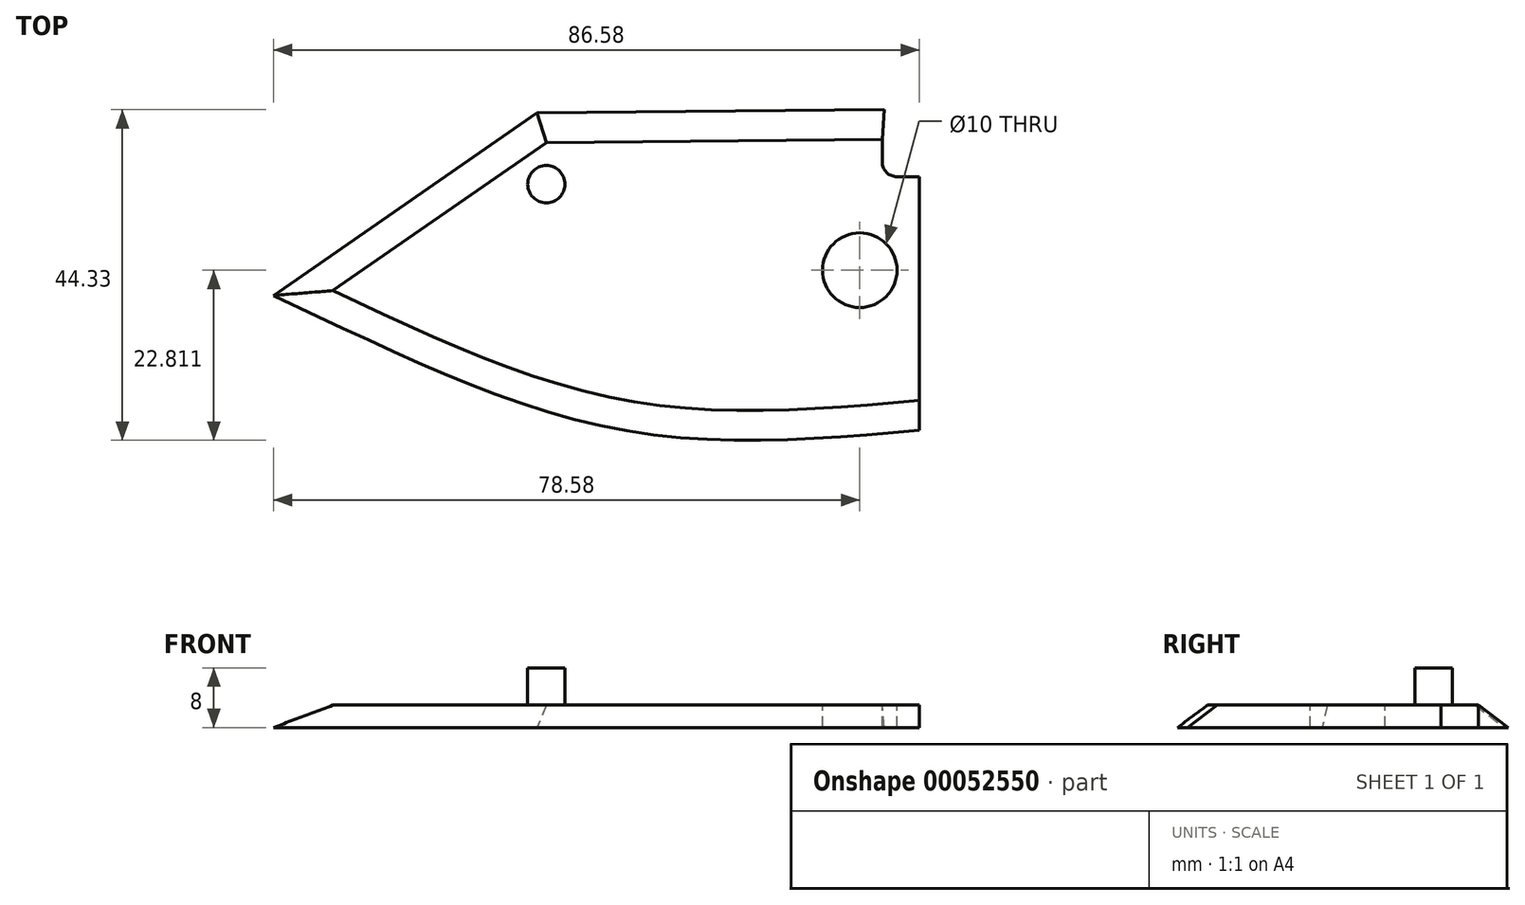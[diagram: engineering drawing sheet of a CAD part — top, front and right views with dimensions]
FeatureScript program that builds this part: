
annotation { "Feature Type Name" : "Feature", "Feature Type Description" : "" }
export const myFeature = defineFeature(function(context is Context, id is Id, definition is map)
    precondition{}
    {
        {
            var Q0;
            Q0=qCreatedBy(makeId("Top.planeOp"),FACE);
            var sketch = newSketch(context, id + "F0", { "sketchPlane" : qUnion([Q0])});
            skLineSegment(sketch, "E0", {"start": v(-5, 35) * mm, "end": v(-50, 34.58) * mm});
            skLineSegment(sketch, "E1", {"start": v(-50, 34.58) * mm, "end": v(-78.63, 14.74) * mm});
            skFitSpline(sketch, "E2", {"points": [v(-78.63, 14.74) * mm, v(-39.25, 0) * mm, v(0, 0) * mm], "startDerivative": vector(77.58, -36.48) * mm, "endDerivative": vector(80.57, 7.12) * mm});
            skLineSegment(sketch, "E3", {"start": v(0, 0) * mm, "end": v(0, 30) * mm});
            skLineSegment(sketch, "E4", {"start": v(0, 30) * mm, "end": v(-3, 30) * mm});
            skLineSegment(sketch, "E5", {"start": v(-5, 32) * mm, "end": v(-5, 35) * mm});
            skPoint(sketch, "E6.visualSharp", {"position": v(-5, 30) * mm});
            skArc(sketch, "E6.filletArc", {"start": v(-5, 32) * mm, "mid": v(-4.41, 30.59) * mm, "end": v(-3, 30) * mm});
            skSolve(sketch);
        }
        {
            var Q0;
            Q0=qCreatedBy(makeId("Right.planeOp"),FACE);
            var sketch = newSketch(context, id + "F1", { "sketchPlane" : qUnion([Q0])});
            skLineSegment(sketch, "E7", {"start": v(0, 0) * mm, "end": v(-4, 0) * mm});
            skLineSegment(sketch, "E8", {"start": v(-4, 0) * mm, "end": v(0, 3) * mm});
            skLineSegment(sketch, "E9", {"start": v(0, 0) * mm, "end": v(0, 3) * mm});
            skSolve(sketch);
        }
        {
            var Q0;
            Q0=makeQuery(id+"F1.imprint","IMPRINT",FACE,{"disambiguationData":[TD([[makeQuery(id+"F1.imprint","IMPRINT",EDGE,{"derivedFrom":sQuery(id+"F1.wireOp",EDGE,"E7")}),-1.0]])]});
            var Q1;
            Q1=sQuery(id+"F0.wireOp",EDGE,"E2");
            var Q2;
            Q2=sQuery(id+"F0.wireOp",EDGE,"E1");
            var Q3;
            Q3=sQuery(id+"F0.wireOp",EDGE,"E0");
            sweep(context, id + "F2", {"profiles" : qUnion([Q0]), "path" : qUnion([Q1, Q2, Q3])});
        }
        {
            var Q0;
            Q0 = qSketchRegion(id + "F0", true);
            extrude(context, id + "F3", {"entities" : qUnion([Q0]), "operationType" : NewBodyOperationType.ADD, "depth" : 3 * mm});
        }
        {
            var Q0;
            Q0=makeQuery(id+"F3.opExtrude","CAP_FACE",FACE,{"disambiguationData":[OSD([sQuery(id+"F0.wireOp",EDGE,"ca5b04ca-4ff3-4a42-8b16-5efeb9b8746d"),sQuery(id+"F0.wireOp",EDGE,"E0"),sQuery(id+"F0.wireOp",EDGE,"E1"),sQuery(id+"F0.wireOp",EDGE,"E2")])],"isStart":false});
            var sketch = newSketch(context, id + "F4", { "sketchPlane" : qUnion([Q0])});
            skCircle(sketch, "E10", {"center": v(-8, 17.47) * mm, "radius": 5 * mm});
            skSolve(sketch);
        }
        {
            var Q0;
            Q0=makeQuery(id+"F4.imprint","IMPRINT",FACE,{"disambiguationData":[TD([[makeQuery(id+"F4.imprint","IMPRINT",EDGE,{"derivedFrom":sQuery(id+"F4.wireOp",EDGE,"E10")}),1.0]])]});
            extrude(context, id + "F5", {"entities" : qUnion([Q0]), "operationType" : NewBodyOperationType.REMOVE, "oppositeDirection" : true, "depth" : 25 * mm});
        }
        {
            var Q0;
            Q0=makeQuery(id+"F3.opExtrude","CAP_FACE",FACE,{"disambiguationData":[OSD([sQuery(id+"F0.wireOp",EDGE,"ca5b04ca-4ff3-4a42-8b16-5efeb9b8746d"),sQuery(id+"F0.wireOp",EDGE,"E0"),sQuery(id+"F0.wireOp",EDGE,"E1"),sQuery(id+"F0.wireOp",EDGE,"E2")])],"isStart":false});
            var sketch = newSketch(context, id + "F6", { "sketchPlane" : qUnion([Q0])});
            skCircle(sketch, "E11", {"center": v(-50, 29) * mm, "radius": 2.5 * mm});
            skSolve(sketch);
        }
        {
            var Q0;
            Q0 = qSketchRegion(id + "F6", true);
            extrude(context, id + "F7", {"entities" : qUnion([Q0]), "operationType" : NewBodyOperationType.ADD, "depth" : 5 * mm});
        }
    });
